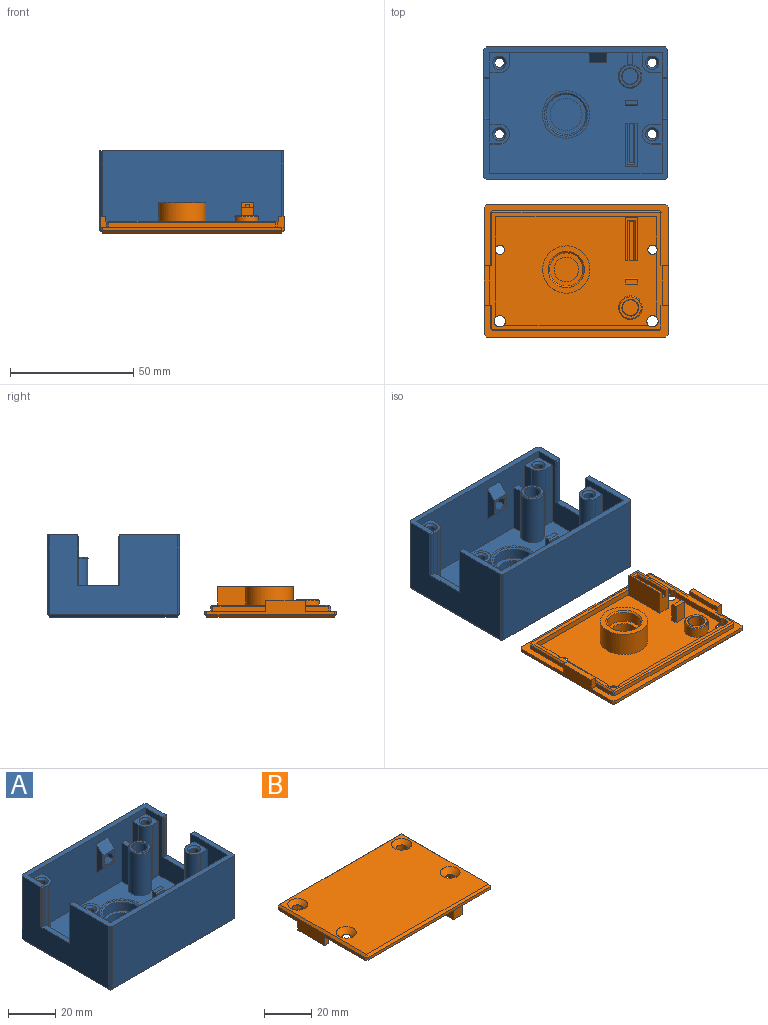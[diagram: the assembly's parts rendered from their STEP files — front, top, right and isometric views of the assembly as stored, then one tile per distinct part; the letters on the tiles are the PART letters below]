
ASSEMBLY  parts=2 mates=1
PART A: 120 faces, bbox 74.8x53.8x33.4 mm
  f0: plane 49x31mm, normal (-1,0,0), area 634.4mm2, adj f3,f4,f17,f19,f21,f23,f42,f43
  f1: plane 51.8x32.4mm, normal (1,0,0), area 1199.7mm2, adj f17,f21,f23,f81,f82,f83,f84,f85
  f2: plane 7x7mm, normal (0,-1,0), area 27.3mm2, adj f66,f67,f68,f69,f70,f71,f72,f73
  f3: plane 70x49mm, normal (0,0,1), area 2721.3mm2, adj f0,f4,f5,f16,f19,f25,f33,f34
  f4: plane 70x31mm, normal (0,-1,0), area 1569mm2, adj f0,f3,f16,f17,f33,f34,f35,f38
  f5: cylinder r=4.8mm len=21.6mm, axis (0,0,-1), area 602.9mm2, adj f3,f33,f34,f35,f113
  f6: plane 51.8x32.4mm, normal (-1,0,0), area 1325.7mm2, adj f17,f21,f22,f90,f94,f96,f103,f106
  f7: plane 72.8x32.4mm, normal (0,-1,0), area 2358.7mm2, adj f21,f87,f93,f96
  f8: cylinder r=1.9mm len=29.6mm, axis (0,0,1), area 353.4mm2, adj f13,f110
  f9: cylinder r=1.9mm len=29.6mm, axis (0,0,1), area 353.4mm2, adj f13,f111
  f10: cylinder r=1.9mm len=29.6mm, axis (0,0,1), area 353.4mm2, adj f13,f112
  f11: plane 72.8x32.4mm, normal (0,1,0), area 2358.7mm2, adj f17,f85,f89,f90
  f12: cylinder r=1.9mm len=29.6mm, axis (0,0,1), area 353.4mm2, adj f13,f109
  f13: plane 72.8x51.8mm, normal (0,0,-1), area 3725.7mm2, adj f8,f9,f10,f12,f88,f89,f93,f94
  f14: plane 19.9x1.2mm, normal (0,-1,0), area 23.9mm2, adj f23,f97,f98,f99
  f15: plane 19.9x1.2mm, normal (0,-1,0), area 23.9mm2, adj f22,f106,f107,f108
  f16: plane 49x31mm, normal (1,0,0), area 718.4mm2, adj f3,f4,f17,f19,f21,f22,f36,f39
  f17: plane 74.8x12.3mm, normal (0,0,1), area 226mm2, adj f0,f1,f4,f6,f11,f16,f85,f90
  f18: plane 19.9x1.2mm, normal (0,1,0), area 23.9mm2, adj f23,f100,f101,f102
  f19: plane 70x31mm, normal (0,1,0), area 2170mm2, adj f0,f3,f16,f21
  f20: plane 19.9x1.2mm, normal (0,1,0), area 23.9mm2, adj f22,f103,f104,f105
  f21: plane 74.8x24.3mm, normal (0,0,1), area 283.6mm2, adj f0,f1,f6,f7,f16,f19,f87,f96
  f22: plane 17.2x2.4mm, normal (0,0,1), area 39.1mm2, adj f6,f15,f16,f20,f103,f104,f106,f107
  f23: plane 17.2x2.4mm, normal (0,0,1), area 39.1mm2, adj f0,f1,f14,f18,f97,f98,f100,f101
  f24: cylinder r=8.15mm len=16.3mm, axis (0,0,-1), area 225.3mm2, adj f29,f115
  f25: cylinder r=9.6mm len=19.2mm, axis (0,0,-1), area 542.9mm2, adj f3,f26
  f26: plane 19.2x19.2mm, normal (0,0,1), area 49mm2, adj f25,f115
  f27: plane 13x13mm, normal (0,0,1), area 132.7mm2, adj f28
  f28: cylinder r=6.5mm len=13mm, axis (0,0,-1), area 204.2mm2, adj f27,f29
  f29: plane 16.3x16.3mm, normal (0,0,1), area 75.9mm2, adj f24,f28
  f30: cylinder r=3.2mm len=21.8mm, axis (0,0,-1), area 438.3mm2, adj f32,f114
  f31: plane 8.8x8.8mm, normal (0,0,1), area 24.5mm2, adj f113,f114
  f32: plane 6.4x6.4mm, normal (0,0,1), area 32.2mm2, adj f30
  f33: plane 20x4.85mm, normal (1,0,0), area 97mm2, adj f3,f4,f5,f35
  f34: plane 20x4.85mm, normal (-1,0,0), area 97mm2, adj f3,f4,f5,f35
  f35: plane 4.85x2.4mm, normal (0,0,1), area 11.4mm2, adj f4,f5,f33,f34
  f36: plane 28x4mm, normal (0,-1,0), area 112mm2, adj f3,f16,f37,f39
  f37: cylinder r=4mm len=28mm, axis (0,0,-1), area 175.9mm2, adj f3,f36,f38,f39
  f38: plane 28x4mm, normal (1,0,0), area 112mm2, adj f3,f4,f37,f39
  f39: plane 8x8mm, normal (0,0,1), area 37.7mm2, adj f4,f16,f36,f37,f38,f112
  f40: plane 28x4mm, normal (-1,0,0), area 112mm2, adj f3,f4,f41,f43
  f41: cylinder r=4mm len=28mm, axis (0,0,-1), area 175.9mm2, adj f3,f40,f42,f43
  f42: plane 28x4mm, normal (0,-1,0), area 112mm2, adj f0,f3,f41,f43
  f43: plane 8x8mm, normal (0,0,1), area 37.7mm2, adj f0,f4,f40,f41,f42,f111
  f44: plane 28x4mm, normal (0,1,0), area 112mm2, adj f3,f16,f46,f47
  f45: plane 28x4mm, normal (0,-1,0), area 112mm2, adj f3,f16,f46,f47
  f46: cylinder r=4mm len=28mm, axis (0,0,-1), area 351.9mm2, adj f3,f44,f45,f47
  f47: plane 8x8mm, normal (0,0,1), area 34.2mm2, adj f16,f44,f45,f46,f110
  f48: plane 28x4mm, normal (0,1,0), area 112mm2, adj f0,f3,f49,f51
  f49: cylinder r=4mm len=28mm, axis (0,0,-1), area 351.9mm2, adj f3,f48,f50,f51
  f50: plane 28x4mm, normal (0,-1,0), area 112mm2, adj f0,f3,f49,f51
  f51: plane 8x8mm, normal (0,0,1), area 34.2mm2, adj f0,f48,f49,f50,f109
  f52: plane 7x5mm, normal (0,1,0), area 29.2mm2, adj f3,f53,f54,f56,f57,f59,f60,f116
  f53: plane 16x1.8mm, normal (0,0,1), area 28.8mm2, adj f52,f54,f55,f56
  f54: plane 16x2.4mm, normal (1,0,0), area 38.4mm2, adj f52,f53,f55,f116
  f55: plane 2.4x1.8mm, normal (0,1,0), area 4.3mm2, adj f53,f54,f56,f118
  f56: plane 16x2.4mm, normal (-1,0,0), area 38.4mm2, adj f52,f53,f55,f117
  f57: plane 17.6x7mm, normal (-1,0,0), area 123.2mm2, adj f3,f52,f58,f60
  f58: plane 7x5mm, normal (0,-1,0), area 35mm2, adj f3,f57,f59,f60
  f59: plane 17.6x7mm, normal (1,0,0), area 123.2mm2, adj f3,f52,f58,f60
  f60: plane 17.6x5mm, normal (0,0,1), area 38.2mm2, adj f52,f57,f58,f59,f116,f117,f118
  f61: plane 5x2.4mm, normal (-1,0,0), area 11.8mm2, adj f3,f62,f64,f65,f119
  f62: plane 5x4.4mm, normal (0,-1,0), area 22mm2, adj f3,f61,f63,f119
  f63: plane 5x2.4mm, normal (1,0,0), area 11.8mm2, adj f3,f62,f64,f65,f119
  f64: plane 5x5mm, normal (0,1,0), area 25mm2, adj f3,f61,f63,f65
  f65: plane 5x1.8mm, normal (0,0,1), area 9mm2, adj f61,f63,f64,f119
  f66: plane 15x4mm, normal (1,0,0), area 44mm2, adj f2,f4,f68,f69
  f67: plane 15x4mm, normal (-1,0,0), area 44mm2, adj f2,f4,f68,f69
  f68: plane 7x4mm, normal (0,-0.71,0.71), area 39.6mm2, adj f2,f4,f66,f67
  f69: plane 7x4mm, normal (0,-0.71,-0.71), area 39.6mm2, adj f2,f4,f66,f67
  f70: plane 4x2.5mm, normal (0.5,0,0.87), area 11.5mm2, adj f2,f71,f75,f76
  f71: plane 4x2.5mm, normal (-0.5,0,0.87), area 11.5mm2, adj f2,f70,f72,f76
  f72: plane 4x2.89mm, normal (-1,0,0), area 11.5mm2, adj f2,f71,f73,f76
  f73: plane 4x2.5mm, normal (-0.5,0,-0.87), area 11.5mm2, adj f2,f72,f74,f76
  f74: plane 4x2.5mm, normal (0.5,0,-0.87), area 11.5mm2, adj f2,f73,f75,f76
  f75: plane 4x2.89mm, normal (1,0,0), area 11.5mm2, adj f2,f70,f74,f76
  f76: plane 5.77x5mm, normal (0,-1,0), area 21.7mm2, adj f70,f71,f72,f73,f74,f75
  f77: plane 7x1.4mm, normal (0,0,-1), area 9.8mm2, adj f0,f78,f80,f84
  f78: plane 12x1.4mm, normal (0,1,0), area 16.8mm2, adj f0,f77,f79,f83
  f79: plane 7x1.4mm, normal (0,0,1), area 9.8mm2, adj f0,f78,f80,f81
  f80: plane 12x1.4mm, normal (0,-1,0), area 16.8mm2, adj f0,f77,f79,f82
  f81: plane 9x1mm, normal (0.71,0,0.71), area 11.3mm2, adj f1,f79,f82,f83
  f82: plane 14x1mm, normal (0.71,-0.71,0), area 18.4mm2, adj f1,f80,f81,f84
  f83: plane 14x1mm, normal (0.71,0.71,0), area 18.4mm2, adj f1,f78,f81,f84
  f84: plane 9x1mm, normal (0.71,0,-0.71), area 11.3mm2, adj f1,f77,f82,f83
  f85: plane 32.4x1mm, normal (0.71,0.71,0), area 45.8mm2, adj f1,f11,f17,f86
  f86: plane 1x1mm, normal (0.58,0.58,-0.58), area 0.9mm2, adj f85,f88,f89
  f87: plane 32.4x1mm, normal (0.71,-0.71,0), area 45.8mm2, adj f1,f7,f21,f91
  f88: plane 51.8x1mm, normal (0.71,0,-0.71), area 73.3mm2, adj f1,f13,f86,f91
  f89: plane 72.8x1mm, normal (0,0.71,-0.71), area 103mm2, adj f11,f13,f86,f92
  f90: plane 32.4x1mm, normal (-0.71,0.71,0), area 45.8mm2, adj f6,f11,f17,f92
  f91: plane 1x1mm, normal (0.58,-0.58,-0.58), area 0.9mm2, adj f87,f88,f93
  f92: plane 1x1mm, normal (-0.58,0.58,-0.58), area 0.9mm2, adj f89,f90,f94
  f93: plane 72.8x1mm, normal (0,-0.71,-0.71), area 103mm2, adj f7,f13,f91,f95
  f94: plane 51.8x1mm, normal (-0.71,0,-0.71), area 73.3mm2, adj f6,f13,f92,f95
  f95: plane 1x1mm, normal (-0.58,-0.58,-0.58), area 0.9mm2, adj f93,f94,f96
  f96: plane 32.4x1mm, normal (-0.71,-0.71,0), area 45.8mm2, adj f6,f7,f21,f95
  f97: plane 20.5x0.6mm, normal (0.71,-0.71,0), area 17.1mm2, adj f1,f14,f23,f99
  f98: plane 20.5x0.6mm, normal (-0.71,-0.71,0), area 17.1mm2, adj f0,f14,f23,f99
  f99: plane 2.4x0.6mm, normal (0,-0.71,0.71), area 1.5mm2, adj f14,f17,f97,f98
  f100: plane 20.5x0.6mm, normal (0.71,0.71,0), area 17.1mm2, adj f1,f18,f23,f102
  f101: plane 20.5x0.6mm, normal (-0.71,0.71,0), area 17.1mm2, adj f0,f18,f23,f102
  f102: plane 2.4x0.6mm, normal (0,0.71,0.71), area 1.5mm2, adj f18,f21,f100,f101
  f103: plane 20.5x0.6mm, normal (-0.71,0.71,0), area 17.1mm2, adj f6,f20,f22,f105
  f104: plane 20.5x0.6mm, normal (0.71,0.71,0), area 17.1mm2, adj f16,f20,f22,f105
  f105: plane 2.4x0.6mm, normal (0,0.71,0.71), area 1.5mm2, adj f20,f21,f103,f104
  f106: plane 20.5x0.6mm, normal (-0.71,-0.71,0), area 17.1mm2, adj f6,f15,f22,f108
  f107: plane 20.5x0.6mm, normal (0.71,-0.71,0), area 17.1mm2, adj f15,f16,f22,f108
  f108: plane 2.4x0.6mm, normal (0,-0.71,0.71), area 1.5mm2, adj f15,f17,f106,f107
  f109: cone r=1.9mm half-angle=45deg, axis (0,0,1), area 16.3mm2, adj f12,f51
  f110: cone r=1.9mm half-angle=45deg, axis (0,0,1), area 16.3mm2, adj f8,f47
  f111: cone r=1.9mm half-angle=45deg, axis (0,0,1), area 16.3mm2, adj f9,f43
  f112: cone r=1.9mm half-angle=45deg, axis (0,0,1), area 16.3mm2, adj f10,f39
  f113: cone r=4.4mm half-angle=45deg, axis (0,0,-1), area 16.3mm2, adj f5,f31
  f114: cone r=3mm half-angle=45deg, axis (0,0,1), area 5.9mm2, adj f30,f31
  f115: cone r=8.15mm half-angle=45deg, axis (0,0,1), area 45.1mm2, adj f24,f26
  f116: plane 16.6x0.6mm, normal (0.71,0,0.71), area 13.8mm2, adj f52,f54,f60,f118
  f117: plane 16.6x0.6mm, normal (-0.71,0,0.71), area 13.8mm2, adj f52,f56,f60,f118
  f118: plane 3x0.6mm, normal (0,0.71,0.71), area 2mm2, adj f55,f60,f116,f117
  f119: plane 5x0.6mm, normal (0,-0.71,0.71), area 4.2mm2, adj f61,f62,f63,f65
PART B: 90 faces, bbox 74.8x53.8x12.4 mm
  f0: plane 65.2x44.2mm, normal (0,0,-1), area 2371.2mm2, adj f6,f7,f8,f9,f13,f19,f22,f24
  f1: plane 74.8x12.9mm, normal (0,0,-1), area 247.7mm2, adj f3,f4,f10,f36,f40,f48,f51,f52
  f2: plane 74.8x24.9mm, normal (0,0,-1), area 310.1mm2, adj f4,f5,f10,f38,f41,f49,f50,f59
  f3: plane 72.8x1.4mm, normal (0,1,0), area 101.9mm2, adj f1,f61,f65,f66
  f4: plane 51.8x5.9mm, normal (-1,0,0), area 144.5mm2, adj f1,f2,f40,f41,f43,f61,f63,f64
  f5: plane 72.8x1.4mm, normal (0,-1,0), area 101.9mm2, adj f2,f63,f69,f72
  f6: cylinder r=1.9mm len=3.8mm, axis (0,0,-1), area 6.4mm2, adj f0,f45,f57,f58,f60
  f7: cylinder r=2.3mm len=4.6mm, axis (0,0,-1), area 24.7mm2, adj f0,f47,f53,f58,f60
  f8: cylinder r=1.9mm len=3.8mm, axis (0,0,-1), area 6.4mm2, adj f0,f44,f54,f55,f60
  f9: cylinder r=2.3mm len=4.6mm, axis (0,0,-1), area 24.7mm2, adj f0,f46,f53,f54,f60
  f10: plane 51.8x5.9mm, normal (1,0,0), area 144.5mm2, adj f1,f2,f36,f38,f39,f66,f70,f72
  f11: plane 72.8x51.8mm, normal (0,0,1), area 3549.4mm2, adj f44,f45,f46,f47,f64,f65,f69,f70
  f12: cylinder r=6.75mm len=13.5mm, axis (0,0,1), area 186.6mm2, adj f17,f79
  f13: cylinder r=9.6mm len=19.2mm, axis (0,0,1), area 603.2mm2, adj f0,f14
  f14: plane 19.2x19.2mm, normal (0,0,-1), area 119.8mm2, adj f13,f79
  f15: plane 10x10mm, normal (0,0,-1), area 78.5mm2, adj f16
  f16: cylinder r=5mm len=10mm, axis (0,0,1), area 188.5mm2, adj f15,f17
  f17: plane 13.5x13.5mm, normal (0,0,-1), area 64.6mm2, adj f12,f16
  f18: cylinder r=3.2mm len=6.4mm, axis (0,0,1), area 88.5mm2, adj f21,f74
  f19: cylinder r=4.8mm len=9.6mm, axis (0,0,1), area 126.7mm2, adj f0,f73
  f20: plane 8.8x8.8mm, normal (0,0,-1), area 24.5mm2, adj f73,f74
  f21: plane 6.4x6.4mm, normal (0,0,-1), area 32.2mm2, adj f18
  f22: plane 10x5mm, normal (0,1,0), area 43.9mm2, adj f0,f23,f29,f31,f32,f34,f35,f81
  f23: plane 16x1.8mm, normal (0,0,-1), area 28.8mm2, adj f22,f29,f30,f31
  f24: plane 8x2.4mm, normal (-1,0,0), area 19mm2, adj f0,f25,f27,f28,f80
  f25: plane 7.4x5mm, normal (0,-1,0), area 37mm2, adj f0,f24,f26,f80
  f26: plane 8x2.4mm, normal (1,0,0), area 19mm2, adj f0,f25,f27,f28,f80
  f27: plane 8x5mm, normal (0,1,0), area 40mm2, adj f0,f24,f26,f28
  f28: plane 5x1.8mm, normal (0,0,-1), area 9mm2, adj f24,f26,f27,f80
  f29: plane 16x2.6mm, normal (1,0,0), area 41.6mm2, adj f22,f23,f30,f81
  f30: plane 2.6x1.8mm, normal (0,1,0), area 4.7mm2, adj f23,f29,f31,f83
  f31: plane 16x2.6mm, normal (-1,0,0), area 41.6mm2, adj f22,f23,f30,f82
  f32: plane 17.6x10mm, normal (-1,0,0), area 176mm2, adj f0,f22,f33,f35
  f33: plane 10x5mm, normal (0,-1,0), area 50mm2, adj f0,f32,f34,f35
  f34: plane 17.6x10mm, normal (1,0,0), area 176mm2, adj f0,f22,f33,f35
  f35: plane 17.6x5mm, normal (0,0,-1), area 38.2mm2, adj f22,f32,f33,f34,f81,f82,f83
  f36: plane 4.5x3.2mm, normal (0,1,0), area 11.5mm2, adj f1,f10,f37,f39,f48,f60,f86
  f37: plane 16x2.1mm, normal (-1,0,0), area 33.6mm2, adj f36,f38,f39,f60
  f38: plane 4.5x3.2mm, normal (0,-1,0), area 11.5mm2, adj f2,f10,f37,f39,f50,f60,f89
  f39: plane 16x2.4mm, normal (0,0,-1), area 38.4mm2, adj f10,f36,f37,f38
  f40: plane 4.5x3.2mm, normal (0,1,0), area 11.5mm2, adj f1,f4,f42,f43,f52,f60,f84
  f41: plane 4.5x3.2mm, normal (0,-1,0), area 11.5mm2, adj f2,f4,f42,f43,f49,f60,f87
  f42: plane 16x2.1mm, normal (1,0,0), area 33.6mm2, adj f40,f41,f43,f60
  f43: plane 16x2.4mm, normal (0,0,-1), area 38.4mm2, adj f4,f40,f41,f42
  f44: cone r=1.9mm half-angle=45deg, axis (0,0,1), area 62.3mm2, adj f8,f11
  f45: cone r=1.9mm half-angle=45deg, axis (0,0,1), area 62.3mm2, adj f6,f11
  f46: cone r=1.9mm half-angle=45deg, axis (0,0,1), area 54.9mm2, adj f9,f11
  f47: cone r=1.9mm half-angle=45deg, axis (0,0,1), area 54.9mm2, adj f7,f11
  f48: plane 9.5x1.8mm, normal (1,0,0), area 17.1mm2, adj f1,f36,f75,f86
  f49: plane 21.5x1.8mm, normal (-1,0,0), area 38.7mm2, adj f2,f41,f77,f87
  f50: plane 21.5x1.8mm, normal (1,0,0), area 38.7mm2, adj f2,f38,f78,f89
  f51: plane 68x1.8mm, normal (0,1,0), area 122.4mm2, adj f1,f75,f76,f85
  f52: plane 9.5x1.8mm, normal (-1,0,0), area 17.1mm2, adj f1,f40,f76,f84
  f53: plane 58.7x2.4mm, normal (0,-1,0), area 140.9mm2, adj f0,f7,f9,f60
  f54: plane 26.32x2.4mm, normal (-1,0,0), area 63.2mm2, adj f0,f8,f9,f60
  f55: plane 12.58x2.4mm, normal (-1,0,0), area 30.2mm2, adj f0,f8,f56,f60
  f56: plane 65.2x2.4mm, normal (0,1,0), area 156.5mm2, adj f0,f55,f57,f60
  f57: plane 12.58x2.4mm, normal (1,0,0), area 30.2mm2, adj f0,f6,f56,f60
  f58: plane 26.32x2.4mm, normal (1,0,0), area 63.2mm2, adj f0,f6,f7,f60
  f59: plane 68x1.8mm, normal (0,-1,0), area 122.4mm2, adj f2,f77,f78,f88
  f60: plane 70x47.4mm, normal (0,0,-1), area 378.7mm2, adj f6,f7,f8,f9,f36,f37,f38,f40
  f61: plane 1.4x1mm, normal (-0.71,0.71,0), area 2mm2, adj f1,f3,f4,f62
  f62: plane 1x1mm, normal (-0.58,0.58,0.58), area 0.9mm2, adj f61,f64,f65
  f63: plane 1.4x1mm, normal (-0.71,-0.71,0), area 2mm2, adj f2,f4,f5,f67
  f64: plane 51.8x1mm, normal (-0.71,0,0.71), area 73.3mm2, adj f4,f11,f62,f67
  f65: plane 72.8x1mm, normal (0,0.71,0.71), area 103mm2, adj f3,f11,f62,f68
  f66: plane 1.4x1mm, normal (0.71,0.71,0), area 2mm2, adj f1,f3,f10,f68
  f67: plane 1x1mm, normal (-0.58,-0.58,0.58), area 0.9mm2, adj f63,f64,f69
  f68: plane 1x1mm, normal (0.58,0.58,0.58), area 0.9mm2, adj f65,f66,f70
  f69: plane 72.8x1mm, normal (0,-0.71,0.71), area 103mm2, adj f5,f11,f67,f71
  f70: plane 51.8x1mm, normal (0.71,0,0.71), area 73.3mm2, adj f10,f11,f68,f71
  f71: plane 1x1mm, normal (0.58,-0.58,0.58), area 0.9mm2, adj f69,f70,f72
  f72: plane 1.4x1mm, normal (0.71,-0.71,0), area 2mm2, adj f2,f5,f10,f71
  f73: cone r=4.8mm half-angle=45deg, axis (0,0,1), area 16.3mm2, adj f19,f20
  f74: cone r=3.4mm half-angle=45deg, axis (0,0,-1), area 5.9mm2, adj f18,f20
  f75: plane 2.2x0.8mm, normal (0.71,0.71,0), area 2.3mm2, adj f1,f48,f51,f85,f86
  f76: plane 2.2x0.8mm, normal (-0.71,0.71,0), area 2.3mm2, adj f1,f51,f52,f84,f85
  f77: plane 2.2x0.8mm, normal (-0.71,-0.71,0), area 2.3mm2, adj f2,f49,f59,f87,f88
  f78: plane 2.2x0.8mm, normal (0.71,-0.71,0), area 2.3mm2, adj f2,f50,f59,f88,f89
  f79: cone r=7.35mm half-angle=45deg, axis (0,0,-1), area 37.6mm2, adj f12,f14
  f80: plane 5x0.6mm, normal (0,-0.71,-0.71), area 4.2mm2, adj f24,f25,f26,f28
  f81: plane 16.6x0.6mm, normal (0.71,0,-0.71), area 13.8mm2, adj f22,f29,f35,f83
  f82: plane 16.6x0.6mm, normal (-0.71,0,-0.71), area 13.8mm2, adj f22,f31,f35,f83
  f83: plane 3x0.6mm, normal (0,0.71,-0.71), area 2mm2, adj f30,f35,f81,f82
  f84: plane 9.9x0.6mm, normal (-0.71,0,-0.71), area 8.3mm2, adj f40,f52,f60,f76,f85
  f85: plane 68.8x0.6mm, normal (0,0.71,-0.71), area 58.1mm2, adj f51,f60,f75,f76,f84,f86
  f86: plane 9.9x0.6mm, normal (0.71,0,-0.71), area 8.3mm2, adj f36,f48,f60,f75,f85
  f87: plane 21.9x0.6mm, normal (-0.71,0,-0.71), area 18.4mm2, adj f41,f49,f60,f77,f88
  f88: plane 68.8x0.6mm, normal (0,-0.71,-0.71), area 58.1mm2, adj f59,f60,f77,f78,f87,f89
  f89: plane 21.9x0.6mm, normal (0.71,0,-0.71), area 18.4mm2, adj f38,f50,f60,f78,f88
PLACE A t=(-1.56,30.97,3.73)mm
PLACE B rot(axis=(1,0,0),180deg) t=(-1.44,-31.97,63.73)mm
MATE planar A.f13 <-> B.f11  axis (0,0,-1) through (1.09,31.4,1.33)mm
